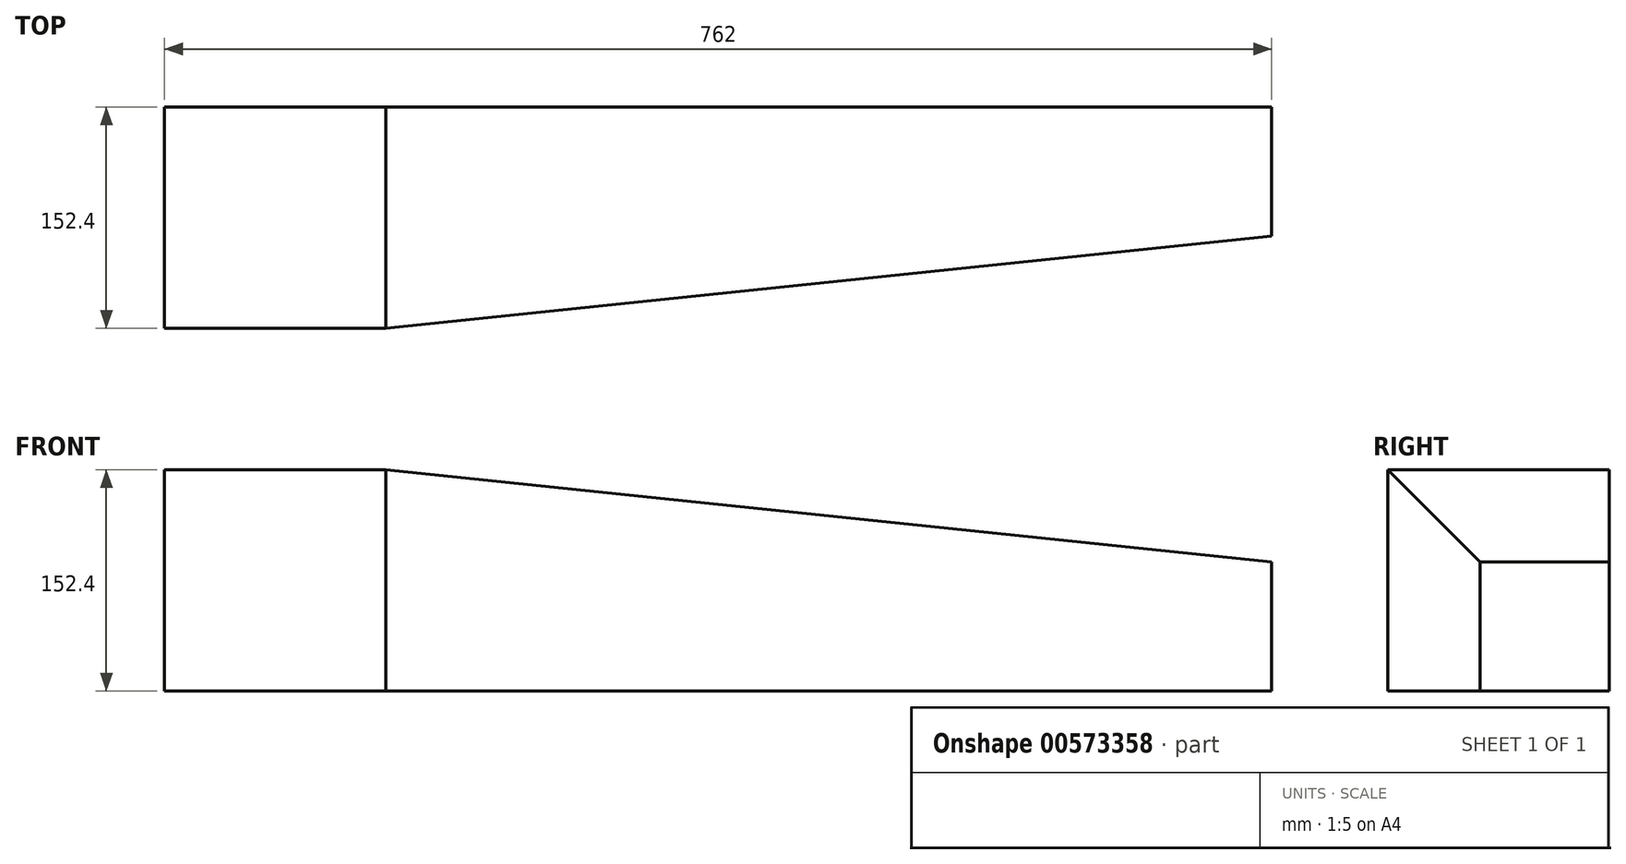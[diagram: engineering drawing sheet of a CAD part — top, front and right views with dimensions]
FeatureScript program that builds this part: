
annotation { "Feature Type Name" : "Feature", "Feature Type Description" : "" }
export const myFeature = defineFeature(function(context is Context, id is Id, definition is map)
    precondition{}
    {
        {
            var Q0;
            Q0=qCreatedBy(makeId("Right.planeOp"),FACE);
            var sketch = newSketch(context, id + "F0", { "sketchPlane" : qUnion([Q0])});
            skLineSegment(sketch, "E0.bottom", {"start": v(-76.2, 76.2) * mm, "end": v(76.2, 76.2) * mm});
            skLineSegment(sketch, "E0.top", {"start": v(-76.2, -76.2) * mm, "end": v(76.2, -76.2) * mm});
            skLineSegment(sketch, "E0.left", {"start": v(-76.2, 76.2) * mm, "end": v(-76.2, -76.2) * mm});
            skLineSegment(sketch, "E0.right", {"start": v(76.2, 76.2) * mm, "end": v(76.2, -76.2) * mm});
            skPoint(sketch, "E0.middle", {"position": v(0, 0) * mm});
            skSolve(sketch);
        }
        {
            var Q0;
            Q0 = qSketchRegion(id + "F0", true);
            extrude(context, id + "F1", {"entities" : qUnion([Q0]), "depth" : 762 * mm, "offsetDistance" : 25.4 * mm});
        }
        {
            var Q0;
            Q0=makeQuery(id+"F1.opExtrude","SWEPT_FACE",FACE,{"disambiguationData":[OSD([sQuery(id+"F0.wireOp",EDGE,"E0.bottom")])]});
            var sketch = newSketch(context, id + "F2", { "sketchPlane" : qUnion([Q0])});
            skLineSegment(sketch, "E1", {"start": v(152.4, -76.2) * mm, "end": v(762, -12.7) * mm});
            skLineSegment(sketch, "E2", {"start": v(152.4, -76.2) * mm, "end": v(762, -76.2) * mm});
            skLineSegment(sketch, "E3", {"start": v(762, -76.2) * mm, "end": v(762, -12.7) * mm});
            skSolve(sketch);
        }
        {
            var Q0;
            Q0 = qSketchRegion(id + "F2", true);
            extrude(context, id + "F3", {"entities" : qUnion([Q0]), "operationType" : NewBodyOperationType.REMOVE, "oppositeDirection" : true, "depth" : 152.4 * mm, "offsetDistance" : 25.4 * mm});
        }
        {
            var Q0;
            Q0=makeQuery(id+"F1.opExtrude","SWEPT_FACE",FACE,{"disambiguationData":[OSD([sQuery(id+"F0.wireOp",EDGE,"E0.right")])]});
            var sketch = newSketch(context, id + "F4", { "sketchPlane" : qUnion([Q0])});
            skLineSegment(sketch, "E4", {"start": v(-152.4, 76.2) * mm, "end": v(-762, 12.7) * mm});
            skSolve(sketch);
        }
        {
            var Q0;
            {var subQ0=sQuery(id+"F4.wireOp",EDGE,"E4");Q0=makeQuery(id+"F4.imprint","IMPRINT",FACE,{"disambiguationData":[TD([[makeQuery(id+"F4.imprint","IMPRINT",EDGE,{"derivedFrom":subQ0}),-1.0]])]});}
            extrude(context, id + "F5", {"entities" : qUnion([Q0]), "operationType" : NewBodyOperationType.REMOVE, "oppositeDirection" : true, "depth" : 152.4 * mm, "offsetDistance" : 25.4 * mm});
        }
    });
